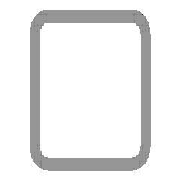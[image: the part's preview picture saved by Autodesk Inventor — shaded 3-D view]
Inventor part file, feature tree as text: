
AUTODESK INVENTOR PART (.ipt)
format: ipt  version: 2025 (Build 290162010, 162A)  size: 131,584 bytes
history: native  units: mm (DEFAULTED — no unit token found)
features: other x4, sketch x1, plane x1
ambient origin geometry x8: Origin, YZ Plane, XZ Plane, XY Plane, X Axis, Y Axis, Z Axis, Center Point
bodies: Solid1 (feature_tree), Body (feature_tree)
feature tree (6):
  parser-record x1  (decoder bookkeeping rows leaked as tree rows — omitted from the tree; the rows remain in map.json)
  other  "Driven Length"
  other  "Start Plane"
  other  "End Plane"
  sketch  "Sketch3"  dims[d3=1420.0mm d4=0.0mm d7=4.0mm d9=40.0mm d11=40.0mm d12=2.0mm d13=40.0mm d14=1460.0mm d15=20.0mm d16=20.0mm d17=90.0deg d18=1420.0mm]
  plane  "Work Plane3"
